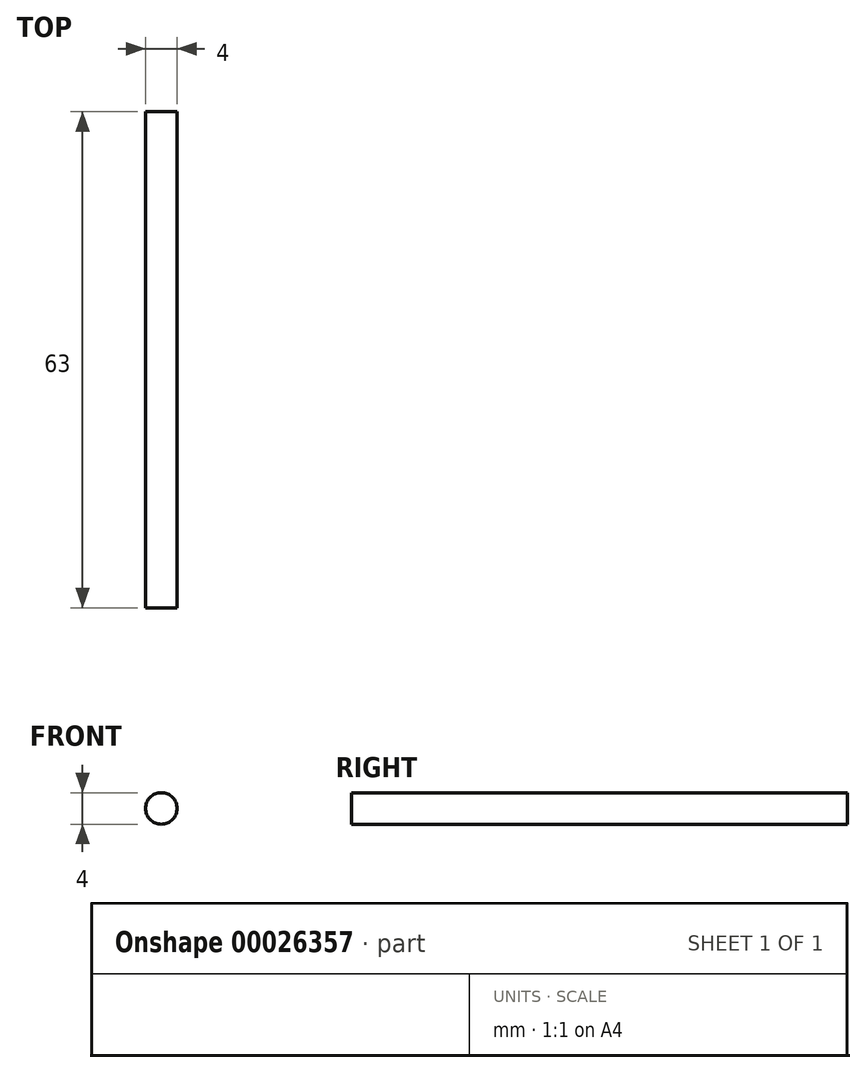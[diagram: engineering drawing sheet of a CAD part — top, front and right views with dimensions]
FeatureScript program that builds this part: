
annotation { "Feature Type Name" : "Feature", "Feature Type Description" : "" }
export const myFeature = defineFeature(function(context is Context, id is Id, definition is map)
    precondition{}
    {
        {
            var Q0;
            Q0=qCreatedBy(makeId("Front.planeOp"),FACE);
            var sketch = newSketch(context, id + "F0", { "sketchPlane" : qUnion([Q0])});
            skCircle(sketch, "E0", {"center": v(-0.46, 0) * mm, "radius": 2 * mm});
            skSolve(sketch);
        }
        {
            var Q0;
            Q0 = qSketchRegion(id + "F0", true);
            extrude(context, id + "F1", {"entities" : qUnion([Q0]), "depth" : 63 * mm});
        }
    });
